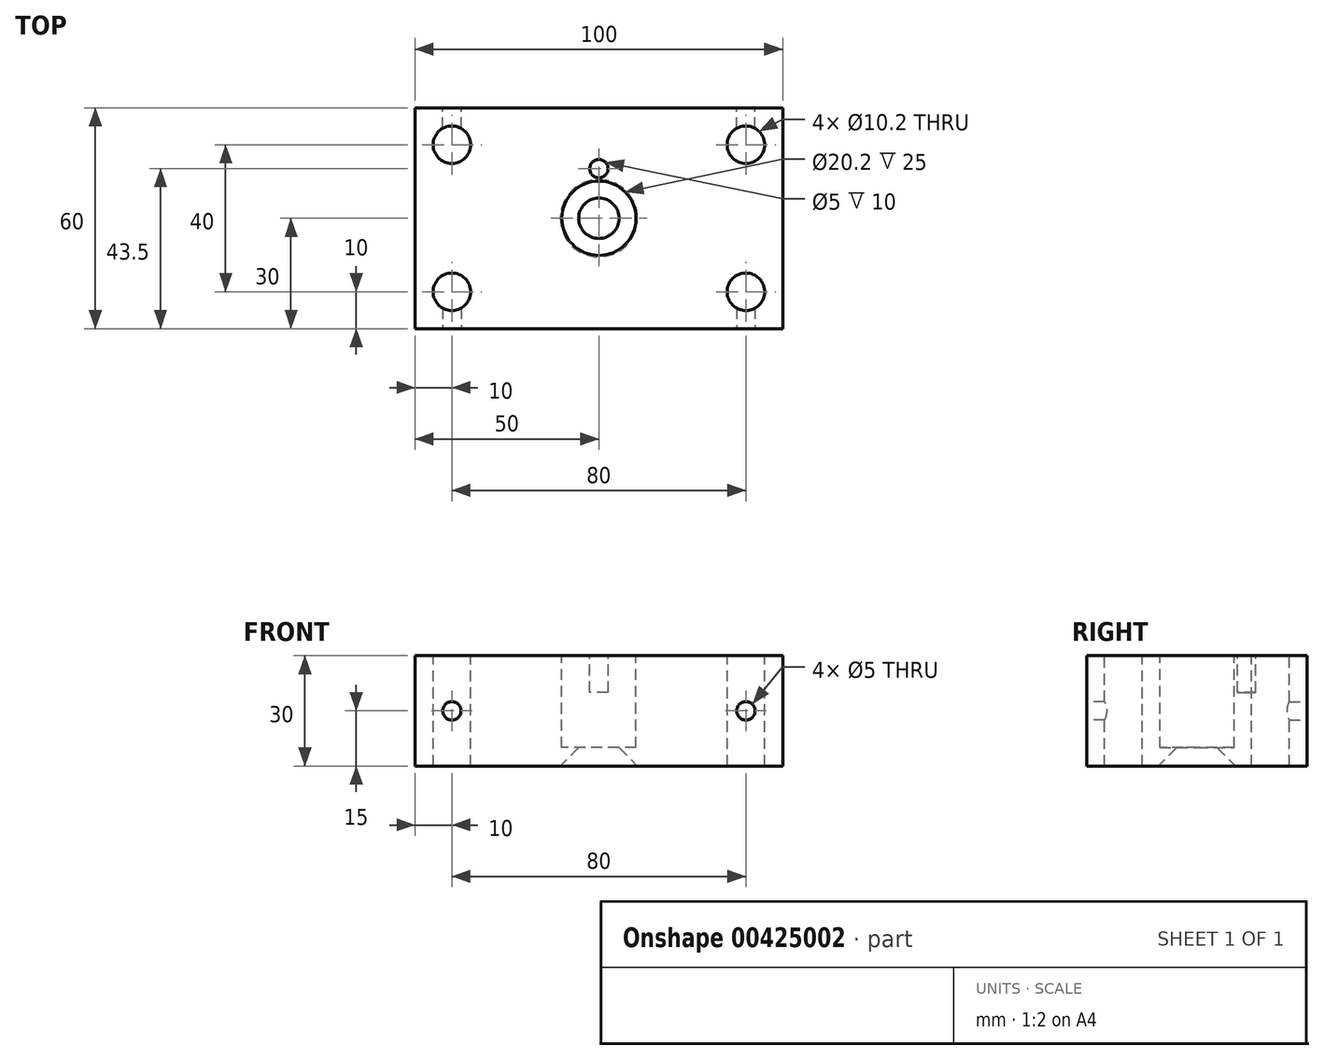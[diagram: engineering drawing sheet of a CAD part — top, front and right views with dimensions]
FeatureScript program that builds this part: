
annotation { "Feature Type Name" : "Feature", "Feature Type Description" : "" }
export const myFeature = defineFeature(function(context is Context, id is Id, definition is map)
    precondition{}
    {
        {
            var Q0;
            Q0=qCreatedBy(makeId("Top.planeOp"),FACE);
            var sketch = newSketch(context, id + "F0", { "sketchPlane" : qUnion([Q0])});
            skLineSegment(sketch, "E0.bottom", {"start": v(-50, 30) * mm, "end": v(50, 30) * mm});
            skLineSegment(sketch, "E0.top", {"start": v(-50, -30) * mm, "end": v(50, -30) * mm});
            skLineSegment(sketch, "E0.left", {"start": v(-50, 30) * mm, "end": v(-50, -30) * mm});
            skLineSegment(sketch, "E0.right", {"start": v(50, 30) * mm, "end": v(50, -30) * mm});
            skSolve(sketch);
        }
        {
            var Q0;
            Q0=makeQuery(id+"F0.imprint","IMPRINT",FACE,{"disambiguationData":[TD([[makeQuery(id+"F0.imprint","IMPRINT",EDGE,{"derivedFrom":sQuery(id+"F0.wireOp",EDGE,"E0.bottom")}),-1.0]])]});
            extrude(context, id + "F1", {"entities" : qUnion([Q0]), "depth" : 30 * mm});
        }
        {
            var Q0;
            Q0=makeQuery(id+"F1.opExtrude","CAP_FACE",FACE,{"disambiguationData":[OSD([sQuery(id+"F0.wireOp",EDGE,"E0.bottom"),sQuery(id+"F0.wireOp",EDGE,"E0.top"),sQuery(id+"F0.wireOp",EDGE,"E0.left"),sQuery(id+"F0.wireOp",EDGE,"E0.right")])],"isStart":false});
            var sketch = newSketch(context, id + "F2", { "sketchPlane" : qUnion([Q0])});
            skCircle(sketch, "E1", {"center": v(0, 0) * mm, "radius": 10.1 * mm});
            skSolve(sketch);
        }
        {
            var Q0;
            Q0=makeQuery(id+"F2.imprint","IMPRINT",FACE,{"disambiguationData":[TD([[makeQuery(id+"F2.imprint","IMPRINT",EDGE,{"derivedFrom":sQuery(id+"F2.wireOp",EDGE,"E1")}),1.0]])]});
            extrude(context, id + "F3", {"entities" : qUnion([Q0]), "operationType" : NewBodyOperationType.REMOVE, "oppositeDirection" : true, "depth" : 25 * mm});
        }
        {
            var Q0;
            Q0=makeQuery(id+"F1.opExtrude","CAP_FACE",FACE,{"disambiguationData":[OSD([sQuery(id+"F0.wireOp",EDGE,"E0.bottom"),sQuery(id+"F0.wireOp",EDGE,"E0.top"),sQuery(id+"F0.wireOp",EDGE,"E0.left"),sQuery(id+"F0.wireOp",EDGE,"E0.right")])],"isStart":false});
            var sketch = newSketch(context, id + "F4", { "sketchPlane" : qUnion([Q0])});
            skCircle(sketch, "E2", {"center": v(-40, 20) * mm, "radius": 5.1 * mm});
            skCircle(sketch, "E3.1.0.0", {"center": v(40, 20) * mm, "radius": 5.1 * mm});
            skLineSegment(sketch, "E3.direction1", {"start": v(-40, 20) * mm, "end": v(40, 20) * mm, "construction": true});
            skCircle(sketch, "E4.1.0.0", {"center": v(-40, -20) * mm, "radius": 5.1 * mm});
            skLineSegment(sketch, "E4.direction1", {"start": v(-40, 20) * mm, "end": v(-40, -20) * mm, "construction": true});
            skCircle(sketch, "E5.1.0.0", {"center": v(40, -20) * mm, "radius": 5.1 * mm});
            skLineSegment(sketch, "E5.direction1", {"start": v(-40, -20) * mm, "end": v(40, -20) * mm, "construction": true});
            skSolve(sketch);
        }
        {
            var Q0;
            Q0=makeQuery(id+"F4.imprint","IMPRINT",FACE,{"disambiguationData":[TD([[makeQuery(id+"F4.imprint","IMPRINT",EDGE,{"derivedFrom":sQuery(id+"F4.wireOp",EDGE,"E2")}),1.0]])]});
            var Q1;
            Q1=makeQuery(id+"F4.imprint","IMPRINT",FACE,{"disambiguationData":[TD([[makeQuery(id+"F4.imprint","IMPRINT",EDGE,{"derivedFrom":sQuery(id+"F4.wireOp",EDGE,"E4.1.0.0")}),1.0]])]});
            var Q2;
            Q2=makeQuery(id+"F4.imprint","IMPRINT",FACE,{"disambiguationData":[TD([[makeQuery(id+"F4.imprint","IMPRINT",EDGE,{"derivedFrom":sQuery(id+"F4.wireOp",EDGE,"E3.1.0.0")}),1.0]])]});
            var Q3;
            Q3=makeQuery(id+"F4.imprint","IMPRINT",FACE,{"disambiguationData":[TD([[makeQuery(id+"F4.imprint","IMPRINT",EDGE,{"derivedFrom":sQuery(id+"F4.wireOp",EDGE,"E5.1.0.0")}),1.0]])]});
            extrude(context, id + "F5", {"entities" : qUnion([Q0, Q1, Q2, Q3]), "operationType" : NewBodyOperationType.REMOVE, "endBound" : BoundingType.THROUGH_ALL, "oppositeDirection" : true, "depth" : 25 * mm});
        }
        {
            var Q0;
            Q0=qCreatedBy(makeId("Right.planeOp"),FACE);
            var sketch = newSketch(context, id + "F6", { "sketchPlane" : qUnion([Q0])});
            skLineSegment(sketch, "E6", {"start": v(0, 0) * mm, "end": v(10.5, 0) * mm});
            skLineSegment(sketch, "E7", {"start": v(10.5, 0) * mm, "end": v(0, 10.5) * mm});
            skLineSegment(sketch, "E8", {"start": v(0, 10.5) * mm, "end": v(0, 0) * mm});
            skSolve(sketch);
        }
        {
            var Q0;
            Q0=qCreatedBy(makeId("Right.planeOp"),FACE);
            var sketch = newSketch(context, id + "F7", { "sketchPlane" : qUnion([Q0])});
            skLineSegment(sketch, "E9", {"start": v(0, 0) * mm, "end": v(0, -46.95) * mm});
            skSolve(sketch);
        }
        {
            var Q0;
            Q0 = qSketchRegion(id + "F6", true);
            var Q1;
            Q1=sQuery(id+"F7.wireOp",EDGE,"E9");
            revolve(context, id + "F8", {"operationType" : NewBodyOperationType.REMOVE, "entities" : qUnion([Q0]), "axis" : qUnion([Q1]), "revolveType" : RevolveType.FULL, "oppositeDirection" : true});
        }
        {
            var Q0;
            Q0=makeQuery(id+"F1.opExtrude","SWEPT_FACE",FACE,{"disambiguationData":[OSD([sQuery(id+"F0.wireOp",EDGE,"E0.bottom")])]});
            var sketch = newSketch(context, id + "F9", { "sketchPlane" : qUnion([Q0])});
            skCircle(sketch, "E10", {"center": v(-40, 15) * mm, "radius": 2.5 * mm});
            skCircle(sketch, "E11", {"center": v(40, 15) * mm, "radius": 2.5 * mm});
            skSolve(sketch);
        }
        {
            var Q0;
            Q0=makeQuery(id+"F9.imprint","IMPRINT",FACE,{"disambiguationData":[TD([[makeQuery(id+"F9.imprint","IMPRINT",EDGE,{"derivedFrom":sQuery(id+"F9.wireOp",EDGE,"E10")}),1.0]])]});
            var Q1;
            Q1=makeQuery(id+"F9.imprint","IMPRINT",FACE,{"disambiguationData":[TD([[makeQuery(id+"F9.imprint","IMPRINT",EDGE,{"derivedFrom":sQuery(id+"F9.wireOp",EDGE,"E11")}),1.0]])]});
            extrude(context, id + "F10", {"entities" : qUnion([Q0, Q1]), "operationType" : NewBodyOperationType.REMOVE, "oppositeDirection" : true, "depth" : 10 * mm});
        }
        {
            var Q0;
            Q0=makeQuery(id+"F1.opExtrude","SWEPT_FACE",FACE,{"disambiguationData":[OSD([sQuery(id+"F0.wireOp",EDGE,"E0.top")])]});
            var sketch = newSketch(context, id + "F11", { "sketchPlane" : qUnion([Q0])});
            skCircle(sketch, "E12", {"center": v(-40, 15) * mm, "radius": 2.5 * mm});
            skCircle(sketch, "E13", {"center": v(40, 15) * mm, "radius": 2.5 * mm});
            skSolve(sketch);
        }
        {
            var Q0;
            Q0=makeQuery(id+"F11.imprint","IMPRINT",FACE,{"disambiguationData":[TD([[makeQuery(id+"F11.imprint","IMPRINT",EDGE,{"derivedFrom":sQuery(id+"F11.wireOp",EDGE,"E12")}),1.0]])]});
            var Q1;
            Q1=makeQuery(id+"F11.imprint","IMPRINT",FACE,{"disambiguationData":[TD([[makeQuery(id+"F11.imprint","IMPRINT",EDGE,{"derivedFrom":sQuery(id+"F11.wireOp",EDGE,"E13")}),1.0]])]});
            extrude(context, id + "F12", {"entities" : qUnion([Q0, Q1]), "operationType" : NewBodyOperationType.REMOVE, "oppositeDirection" : true, "depth" : 10 * mm});
        }
        {
            var Q0;
            Q0=makeQuery(id+"F1.opExtrude","CAP_FACE",FACE,{"disambiguationData":[OSD([sQuery(id+"F0.wireOp",EDGE,"E0.bottom"),sQuery(id+"F0.wireOp",EDGE,"E0.top"),sQuery(id+"F0.wireOp",EDGE,"E0.left"),sQuery(id+"F0.wireOp",EDGE,"E0.right")])],"isStart":false});
            var sketch = newSketch(context, id + "F13", { "sketchPlane" : qUnion([Q0])});
            skCircle(sketch, "E14", {"center": v(0, 13.5) * mm, "radius": 2.5 * mm});
            skSolve(sketch);
        }
        {
            var Q0;
            Q0 = qSketchRegion(id + "F13", true);
            extrude(context, id + "F14", {"entities" : qUnion([Q0]), "operationType" : NewBodyOperationType.REMOVE, "oppositeDirection" : true, "offsetDistance" : 25 * mm, "depth" : 10 * mm});
        }
    });
